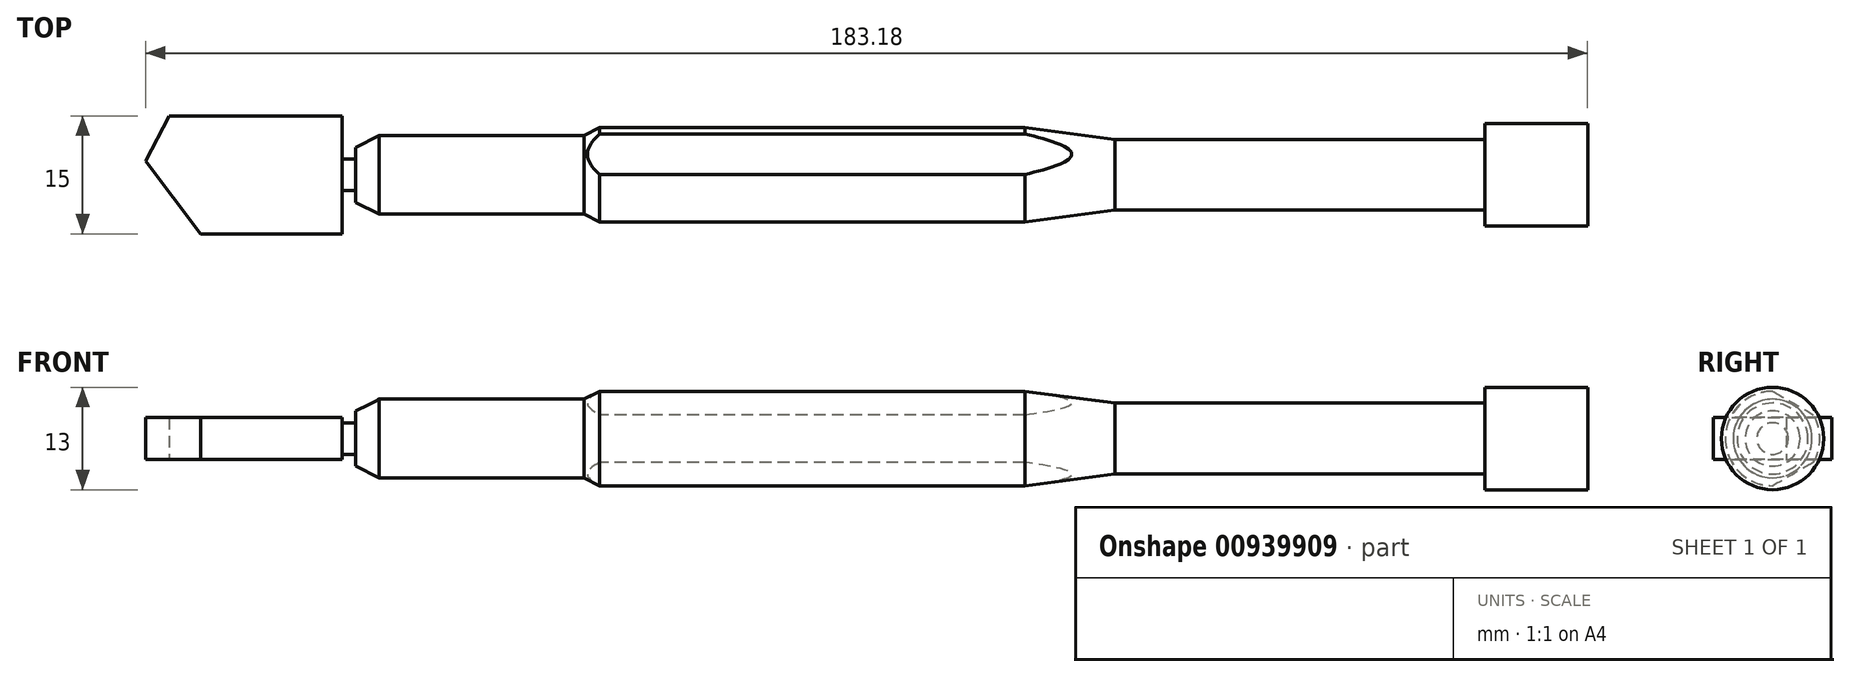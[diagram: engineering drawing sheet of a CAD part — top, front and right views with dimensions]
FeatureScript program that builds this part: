
annotation { "Feature Type Name" : "Feature", "Feature Type Description" : "" }
export const myFeature = defineFeature(function(context is Context, id is Id, definition is map)
    precondition{}
    {
        {
            var Q0;
            Q0=qCreatedBy(makeId("Top.planeOp"),FACE);
            var sketch = newSketch(context, id + "F0", { "sketchPlane" : qUnion([Q0])});
            skLineSegment(sketch, "E0.bottom", {"start": v(-29.66, 7.5) * mm, "end": v(-7.66, 7.5) * mm});
            skLineSegment(sketch, "E0.top", {"start": v(-25.66, -7.5) * mm, "end": v(-7.66, -7.5) * mm});
            skLineSegment(sketch, "E0.right", {"start": v(-7.66, 7.5) * mm, "end": v(-7.66, -7.5) * mm});
            skLineSegment(sketch, "E1", {"start": v(-32.66, 1.76) * mm, "end": v(-29.66, 7.5) * mm});
            skLineSegment(sketch, "E2", {"start": v(-29.66, 7.5) * mm, "end": v(-32.66, 1.76) * mm});
            skLineSegment(sketch, "E3", {"start": v(-25.66, -7.5) * mm, "end": v(-32.66, 1.76) * mm});
            skLineSegment(sketch, "E4", {"start": v(-7.66, -2) * mm, "end": v(-5.96, -2) * mm});
            skLineSegment(sketch, "E5", {"start": v(-5.96, -2) * mm, "end": v(-5.96, 0) * mm});
            skLineSegment(sketch, "E6.bottom", {"start": v(-5.96, -3.5) * mm, "end": v(-2.96, -5) * mm});
            skLineSegment(sketch, "E6.left", {"start": v(-5.96, -3.5) * mm, "end": v(-5.96, 0) * mm});
            skLineSegment(sketch, "E6.right", {"start": v(-2.96, -5) * mm, "end": v(-2.96, 0) * mm});
            skLineSegment(sketch, "E7", {"start": v(23.04, 0) * mm, "end": v(23.04, -5) * mm});
            skLineSegment(sketch, "E8", {"start": v(23.04, -5) * mm, "end": v(-2.96, -5) * mm});
            skLineSegment(sketch, "E9", {"start": v(25.04, 0) * mm, "end": v(25.04, -6) * mm});
            skLineSegment(sketch, "E10", {"start": v(79.04, 0) * mm, "end": v(79.04, -6) * mm});
            skLineSegment(sketch, "E11", {"start": v(79.04, -6) * mm, "end": v(25.04, -6) * mm});
            skLineSegment(sketch, "E12", {"start": v(23.04, -5) * mm, "end": v(25.04, -6) * mm});
            skLineSegment(sketch, "E13", {"start": v(79.04, -6) * mm, "end": v(90.5, -4.5) * mm});
            skLineSegment(sketch, "E14", {"start": v(90.5, 0) * mm, "end": v(90.5, -4.5) * mm});
            skLineSegment(sketch, "E15", {"start": v(137.5, 0) * mm, "end": v(137.5, -4.5) * mm});
            skLineSegment(sketch, "E16", {"start": v(137.5, -4.5) * mm, "end": v(90.5, -4.5) * mm});
            skLineSegment(sketch, "E17", {"start": v(150.52, 0) * mm, "end": v(150.52, -6.5) * mm});
            skLineSegment(sketch, "E18", {"start": v(150.52, -6.5) * mm, "end": v(137.5, -6.5) * mm});
            skLineSegment(sketch, "E19", {"start": v(137.5, -6.5) * mm, "end": v(137.5, -4.5) * mm});
            skLineSegment(sketch, "E20", {"start": v(-7.66, 0) * mm, "end": v(150.52, 0) * mm});
            skLineSegment(sketch, "E21", {"start": v(-67.44, 0) * mm, "end": v(156.5, 0) * mm, "construction": true});
            skSolve(sketch);
        }
        {
            var Q0;
            {var subQ0=sQuery(id+"F0.wireOp",EDGE,"E4");Q0=makeQuery(id+"F0.imprint","IMPRINT",FACE,{"disambiguationData":[TD([[makeQuery(id+"F0.imprint","IMPRINT",EDGE,{"derivedFrom":subQ0}),1.0]])]});}
            var Q1;
            {var subQ0=sQuery(id+"F0.wireOp",EDGE,"E6.right");Q1=makeQuery(id+"F0.imprint","IMPRINT",FACE,{"disambiguationData":[TD([[makeQuery(id+"F0.imprint","IMPRINT",EDGE,{"derivedFrom":subQ0}),-1.0]])]});}
            var Q2;
            {var subQ0=sQuery(id+"F0.wireOp",EDGE,"E7");Q2=makeQuery(id+"F0.imprint","IMPRINT",FACE,{"disambiguationData":[TD([[makeQuery(id+"F0.imprint","IMPRINT",EDGE,{"derivedFrom":subQ0}),1.0]])]});}
            var Q3;
            {var subQ0=sQuery(id+"F0.wireOp",EDGE,"E9");Q3=makeQuery(id+"F0.imprint","IMPRINT",FACE,{"disambiguationData":[TD([[makeQuery(id+"F0.imprint","IMPRINT",EDGE,{"derivedFrom":subQ0}),1.0]])]});}
            var Q4;
            {var subQ0=sQuery(id+"F0.wireOp",EDGE,"E10");Q4=makeQuery(id+"F0.imprint","IMPRINT",FACE,{"disambiguationData":[TD([[makeQuery(id+"F0.imprint","IMPRINT",EDGE,{"derivedFrom":subQ0}),1.0]])]});}
            var Q5;
            {var subQ0=sQuery(id+"F0.wireOp",EDGE,"E14");Q5=makeQuery(id+"F0.imprint","IMPRINT",FACE,{"disambiguationData":[TD([[makeQuery(id+"F0.imprint","IMPRINT",EDGE,{"derivedFrom":subQ0}),1.0]])]});}
            var Q6;
            {var subQ1=sQuery(id+"F0.wireOp",EDGE,"E15");Q6=makeQuery(id+"F0.imprint","IMPRINT",FACE,{"disambiguationData":[TD([[makeQuery(id+"F0.imprint","IMPRINT",EDGE,{"derivedFrom":subQ1}),1.0]])]});}
            var Q7;
            {var subQ5=sQuery(id+"F0.wireOp",EDGE,"E6.bottom");Q7=makeQuery(id+"F0.imprint","IMPRINT",FACE,{"disambiguationData":[TD([[makeQuery(id+"F0.imprint","IMPRINT",EDGE,{"derivedFrom":subQ5}),1.0]])]});}
            var Q8;
            Q8=sQuery(id+"F0.wireOp",EDGE,"E21");
            revolve(context, id + "F1", {"surfaceOperationType" : NewSurfaceOperationType.NEW, "entities" : qUnion([Q0, Q1, Q2, Q3, Q4, Q5, Q6, Q7]), "axis" : qUnion([Q8]), "revolveType" : RevolveType.FULL});
        }
        {
            var Q0;
            {var subQ3=sQuery(id+"F0.wireOp",EDGE,"E0.bottom");Q0=makeQuery(id+"F0.imprint","IMPRINT",FACE,{"disambiguationData":[TD([[makeQuery(id+"F0.imprint","IMPRINT",EDGE,{"derivedFrom":subQ3}),-1.0]])]});}
            extrude(context, id + "F2", {"entities" : qUnion([Q0]), "operationType" : NewBodyOperationType.ADD, "endBound" : BoundingType.SYMMETRIC, "depth" : 5.3 * mm, "offsetDistance" : 25 * mm});
        }
        {
            var Q0;
            Q0=qCreatedBy(makeId("Right.planeOp"),FACE);
            var sketch = newSketch(context, id + "F3", { "sketchPlane" : qUnion([Q0])});
            skLineSegment(sketch, "E22.0", {"start": v(0.01, 6.02) * mm, "end": v(5.22, 3) * mm});
            skLineSegment(sketch, "E22.2", {"start": v(5.21, -3.02) * mm, "end": v(-0.01, -6.02) * mm});
            skLineSegment(sketch, "E23", {"start": v(5.22, 3) * mm, "end": v(8.66, 3) * mm});
            skLineSegment(sketch, "E24", {"start": v(8.66, 3) * mm, "end": v(8.66, -3.02) * mm});
            skLineSegment(sketch, "E25", {"start": v(8.66, -3.02) * mm, "end": v(5.21, -3.02) * mm});
            skLineSegment(sketch, "E26", {"start": v(0.01, 6.02) * mm, "end": v(0.01, 7.7) * mm});
            skLineSegment(sketch, "E27", {"start": v(0.01, 7.7) * mm, "end": v(11.63, 7.7) * mm});
            skLineSegment(sketch, "E28", {"start": v(11.63, 7.7) * mm, "end": v(11.63, -7.9) * mm});
            skLineSegment(sketch, "E29", {"start": v(11.63, -7.9) * mm, "end": v(0.01, -7.9) * mm});
            skLineSegment(sketch, "E30", {"start": v(0.01, -7.9) * mm, "end": v(-0.01, -6.02) * mm});
            skSolve(sketch);
        }
        {
            var Q0;
            Q0=makeQuery(id+"F3.imprint","IMPRINT",FACE,{"disambiguationData":[TD([[makeQuery(id+"F3.imprint","IMPRINT",EDGE,{"derivedFrom":sQuery(id+"F3.wireOp",EDGE,"E22.0")}),1.0]])]});
            extrude(context, id + "F4", {"entities" : qUnion([Q0]), "operationType" : NewBodyOperationType.REMOVE, "depth" : 97.7 * mm, "offsetDistance" : 25 * mm});
        }
    });
